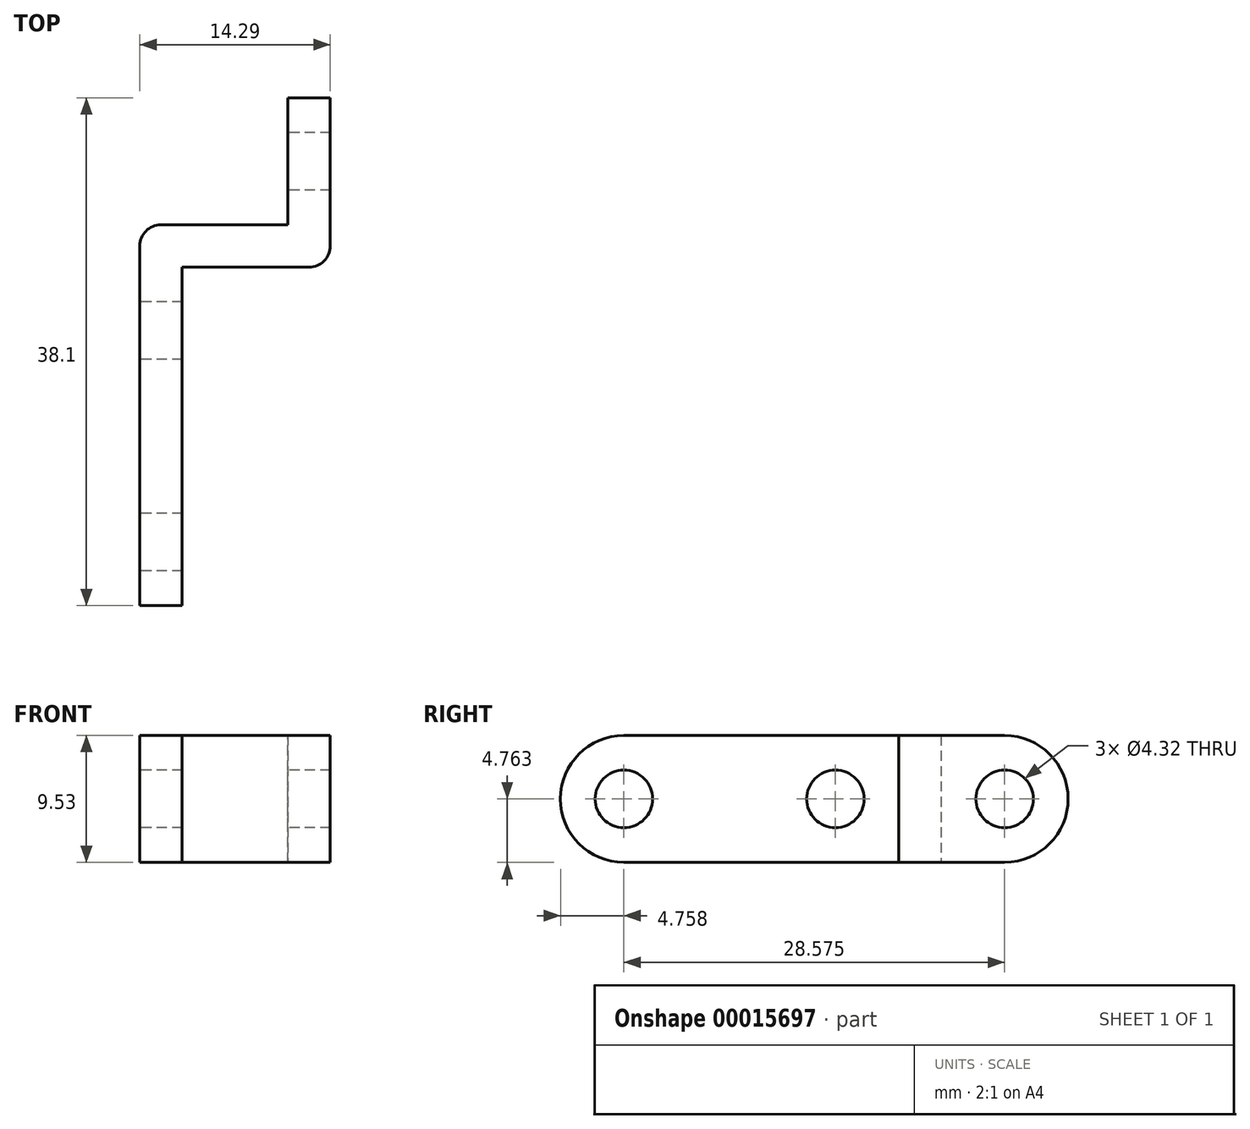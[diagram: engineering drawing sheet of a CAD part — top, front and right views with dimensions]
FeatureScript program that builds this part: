
annotation { "Feature Type Name" : "Feature", "Feature Type Description" : "" }
export const myFeature = defineFeature(function(context is Context, id is Id, definition is map)
    precondition{}
    {
        {
            var Q0;
            Q0=qCreatedBy(makeId("Top.planeOp"),FACE);
            var sketch = newSketch(context, id + "F0", { "sketchPlane" : qUnion([Q0])});
            skLineSegment(sketch, "E0.top", {"start": v(0, -28.58) * mm, "end": v(3.18, -28.58) * mm});
            skLineSegment(sketch, "E0.left", {"start": v(0, 0) * mm, "end": v(0, -28.58) * mm});
            skLineSegment(sketch, "E0.right", {"start": v(3.18, -3.17) * mm, "end": v(3.18, -28.58) * mm});
            skLineSegment(sketch, "E1.bottom", {"start": v(14.29, 9.52) * mm, "end": v(11.11, 9.52) * mm});
            skLineSegment(sketch, "E1.left", {"start": v(14.29, 9.52) * mm, "end": v(14.29, -3.18) * mm});
            skLineSegment(sketch, "E1.right", {"start": v(11.11, 9.52) * mm, "end": v(11.11, 0) * mm});
            skLineSegment(sketch, "E2", {"start": v(0, 0) * mm, "end": v(11.11, 0) * mm});
            skLineSegment(sketch, "E3", {"start": v(3.18, -3.17) * mm, "end": v(14.29, -3.17) * mm});
            skLineSegment(sketch, "E4", {"start": v(5.56, 0) * mm, "end": v(5.56, -3.17) * mm, "construction": true});
            skLineSegment(sketch, "E5", {"start": v(11.11, 0) * mm, "end": v(0, 0) * mm, "construction": true});
            skLineSegment(sketch, "E6", {"start": v(0, 0) * mm, "end": v(0, 0) * mm});
            skSolve(sketch);
        }
        {
            var Q0;
            Q0 = qSketchRegion(id + "F0", true);
            extrude(context, id + "F1", {"entities" : qUnion([Q0]), "depth" : 9.52 * mm});
        }
        {
            var Q0;
            Q0=makeQuery(id+"F1.opExtrude","SWEPT_FACE",FACE,{"disambiguationData":[OSD([sQuery(id+"F0.wireOp",EDGE,"E0.left")])]});
            var sketch = newSketch(context, id + "F2", { "sketchPlane" : qUnion([Q0])});
            skLineSegment(sketch, "E7", {"start": v(-9.52, 4.76) * mm, "end": v(-4.76, 4.76) * mm, "construction": true});
            skLineSegment(sketch, "E8", {"start": v(28.58, 4.76) * mm, "end": v(23.81, 4.76) * mm, "construction": true});
            skLineSegment(sketch, "E9", {"start": v(23.81, 4.76) * mm, "end": v(7.94, 4.76) * mm, "construction": true});
            skLineSegment(sketch, "E10", {"start": v(7.94, 4.76) * mm, "end": v(3.18, 4.76) * mm, "construction": true});
            skCircle(sketch, "E11", {"center": v(-4.76, 4.76) * mm, "radius": 2.16 * mm});
            skCircle(sketch, "E12", {"center": v(7.94, 4.76) * mm, "radius": 2.16 * mm});
            skCircle(sketch, "E13", {"center": v(23.81, 4.76) * mm, "radius": 2.16 * mm});
            skSolve(sketch);
        }
        {
            var Q0;
            Q0 = qSketchRegion(id + "F2", true);
            var Q1;
            Q1=makeQuery(id+"F1.opExtrude","SWEPT_FACE",FACE,{"disambiguationData":[OSD([sQuery(id+"F0.wireOp",EDGE,"E1.left")])]});
            extrude(context, id + "F3", {"entities" : qUnion([Q0]), "operationType" : NewBodyOperationType.REMOVE, "endBound" : BoundingType.UP_TO_SURFACE, "oppositeDirection" : true, "endBoundEntityFace" : qUnion([Q1]), "depth" : 25.4 * mm});
        }
        {
            var Q0;
            Q0=makeQuery(id+"F1.opExtrude","CAP_EDGE",EDGE,{"disambiguationData":[OSD([sQuery(id+"F0.wireOp",EDGE,"E1.bottom")])],"isStart":false});
            var Q1;
            Q1=makeQuery(id+"F1.opExtrude","CAP_EDGE",EDGE,{"disambiguationData":[OSD([sQuery(id+"F0.wireOp",EDGE,"E0.top")])],"isStart":false});
            var Q2;
            Q2=makeQuery(id+"F1.opExtrude","CAP_EDGE",EDGE,{"disambiguationData":[OSD([sQuery(id+"F0.wireOp",EDGE,"E0.top")])],"isStart":true});
            var Q3;
            Q3=makeQuery(id+"F1.opExtrude","CAP_EDGE",EDGE,{"disambiguationData":[OSD([sQuery(id+"F0.wireOp",EDGE,"E1.bottom")])],"isStart":true});
            fillet(context, id + "F4", {"entities" : qUnion([Q0, Q1, Q2, Q3]), "radius" : 4.76 * mm, "tangentPropagation" : true, "allowEdgeOverflow" : false});
        }
        {
            var Q0;
            Q0=makeQuery(id+"F1.opExtrude","SWEPT_EDGE",EDGE,{"disambiguationData":[OSD([sQuery(id+"F0.wireOp",EDGE,"E1.top"),sQuery(id+"F0.wireOp",EDGE,"E1.left"),sQuery(id+"F0.wireOp",EDGE,"E3")])]});
            var Q1;
            Q1=makeQuery(id+"F1.opExtrude","SWEPT_EDGE",EDGE,{"disambiguationData":[OSD([sQuery(id+"F0.wireOp",EDGE,"E0.bottom"),sQuery(id+"F0.wireOp",EDGE,"E0.left"),sQuery(id+"F0.wireOp",EDGE,"E2")])]});
            fillet(context, id + "F5", {"entities" : qUnion([Q0, Q1]), "radius" : 1.59 * mm, "tangentPropagation" : true, "allowEdgeOverflow" : false});
        }
    });
